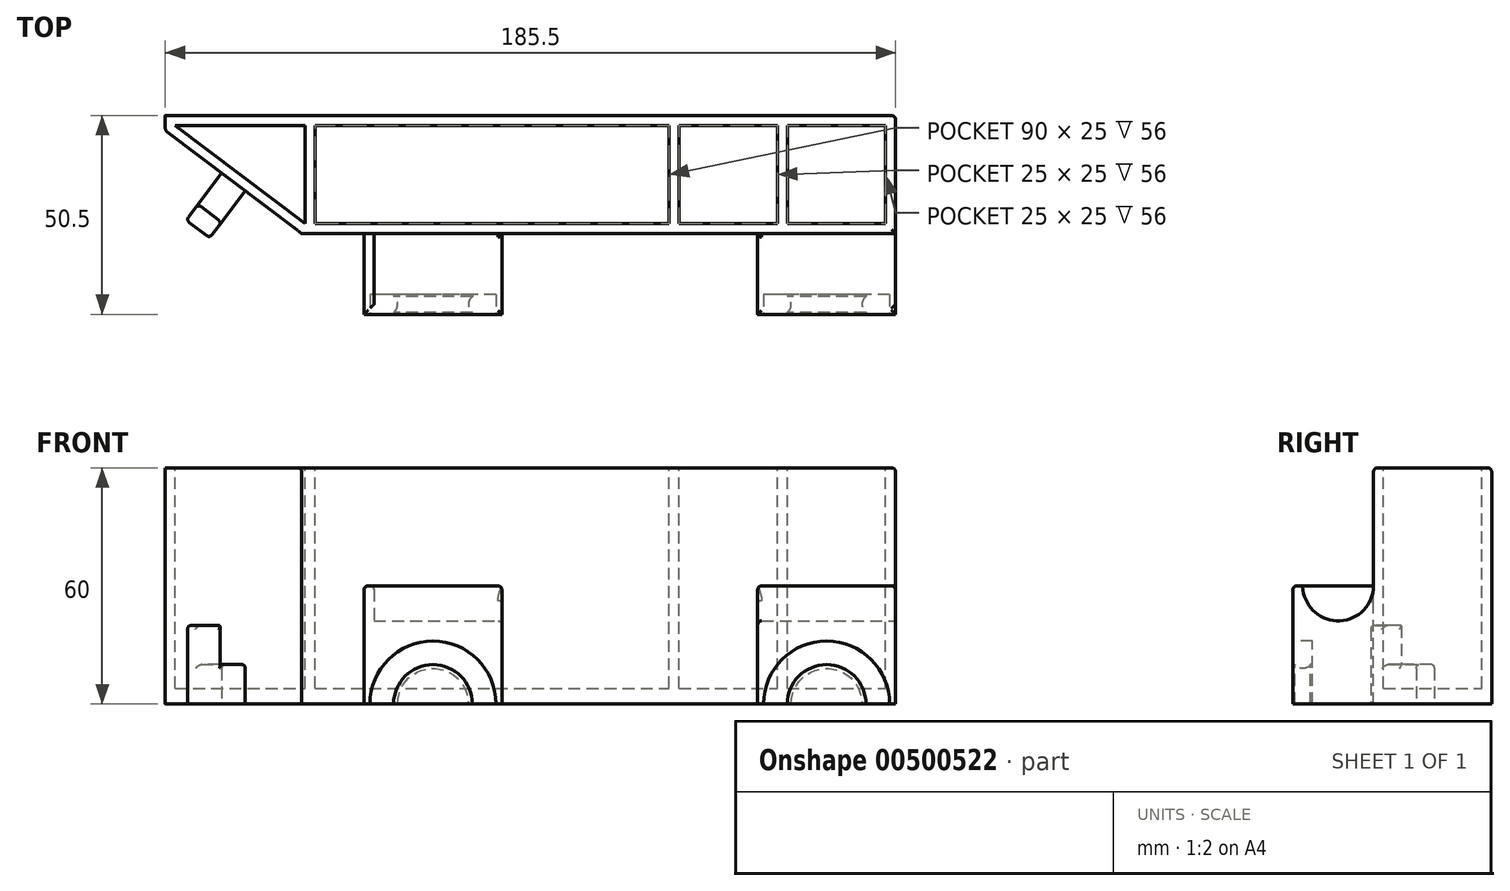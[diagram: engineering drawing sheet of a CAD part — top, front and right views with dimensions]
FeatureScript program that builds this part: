
annotation { "Feature Type Name" : "Feature", "Feature Type Description" : "" }
export const myFeature = defineFeature(function(context is Context, id is Id, definition is map)
    precondition{}
    {
        {
            var Q0;
            Q0=qCreatedBy(makeId("Right.planeOp"),FACE);
            var sketch = newSketch(context, id + "F0", { "sketchPlane" : qUnion([Q0])});
            skLineSegment(sketch, "E0.bottom", {"start": v(0, 0) * mm, "end": v(30, 0) * mm});
            skLineSegment(sketch, "E0.top", {"start": v(0, 60) * mm, "end": v(30, 60) * mm});
            skLineSegment(sketch, "E0.left", {"start": v(0, 0) * mm, "end": v(0, 60) * mm});
            skLineSegment(sketch, "E0.right", {"start": v(30, 0) * mm, "end": v(30, 60) * mm});
            skSolve(sketch);
        }
        {
            var Q0;
            Q0 = qSketchRegion(id + "F0", true);
            extrude(context, id + "F1", {"entities" : qUnion([Q0]), "oppositeDirection" : true, "depth" : 185.5 * mm});
        }
        {
            var Q0;
            Q0=qCreatedBy(makeId("Right.planeOp"),FACE);
            var sketch = newSketch(context, id + "F2", { "sketchPlane" : qUnion([Q0])});
            skLineSegment(sketch, "E1.bottom", {"start": v(0, 0) * mm, "end": v(-20.5, 0) * mm});
            skLineSegment(sketch, "E1.top", {"start": v(0, 30) * mm, "end": v(-20.5, 30) * mm});
            skLineSegment(sketch, "E1.left", {"start": v(0, 0) * mm, "end": v(0, 30) * mm});
            skLineSegment(sketch, "E1.right", {"start": v(-20.5, 0) * mm, "end": v(-20.5, 30) * mm});
            skSolve(sketch);
        }
        {
            var Q0;
            Q0=makeQuery(id+"F2.imprint","IMPRINT",FACE,{"disambiguationData":[TD([[makeQuery(id+"F2.imprint","IMPRINT",EDGE,{"derivedFrom":sQuery(id+"F2.wireOp",EDGE,"E1.bottom")}),-1.0]])]});
            extrude(context, id + "F3", {"entities" : qUnion([Q0]), "operationType" : NewBodyOperationType.ADD, "oppositeDirection" : true, "depth" : 135 * mm});
        }
        {
            var Q0;
            Q0=qCreatedBy(makeId("Top.planeOp"),FACE);
            cPlane(context, id + "F4", {"entities" : qUnion([Q0]), "cplaneType" : CPlaneType.OFFSET, "offset" : 60 * mm, "width" : 150 * mm, "height" : 150 * mm});
        }
        {
            var Q0;
            Q0=qCreatedBy(id+"F4.planeOp",FACE);
            var sketch = newSketch(context, id + "F5", { "sketchPlane" : qUnion([Q0])});
            skLineSegment(sketch, "E2.bottom", {"start": v(-27.5, 27.5) * mm, "end": v(-2.5, 27.5) * mm});
            skLineSegment(sketch, "E2.top", {"start": v(-27.5, 2.5) * mm, "end": v(-2.5, 2.5) * mm});
            skLineSegment(sketch, "E2.left", {"start": v(-27.5, 27.5) * mm, "end": v(-27.5, 2.5) * mm});
            skLineSegment(sketch, "E2.right", {"start": v(-2.5, 27.5) * mm, "end": v(-2.5, 2.5) * mm});
            skLineSegment(sketch, "E3.bottom", {"start": v(-55, 27.5) * mm, "end": v(-30, 27.5) * mm});
            skLineSegment(sketch, "E3.top", {"start": v(-55, 2.5) * mm, "end": v(-30, 2.5) * mm});
            skLineSegment(sketch, "E3.left", {"start": v(-55, 27.5) * mm, "end": v(-55, 2.5) * mm});
            skLineSegment(sketch, "E3.right", {"start": v(-30, 27.5) * mm, "end": v(-30, 2.5) * mm});
            skLineSegment(sketch, "E4.bottom", {"start": v(-147.5, 27.5) * mm, "end": v(-57.5, 27.5) * mm});
            skLineSegment(sketch, "E4.top", {"start": v(-147.5, 2.5) * mm, "end": v(-57.5, 2.5) * mm});
            skLineSegment(sketch, "E4.left", {"start": v(-147.5, 27.5) * mm, "end": v(-147.5, 2.5) * mm});
            skLineSegment(sketch, "E4.right", {"start": v(-57.5, 27.5) * mm, "end": v(-57.5, 2.5) * mm});
            skLineSegment(sketch, "E5", {"start": v(-183, 27.5) * mm, "end": v(-150, 27.5) * mm});
            skLineSegment(sketch, "E6", {"start": v(-150, 27.5) * mm, "end": v(-150, 2.5) * mm});
            skLineSegment(sketch, "E7", {"start": v(-150, 2.5) * mm, "end": v(-183, 27.5) * mm});
            skSolve(sketch);
        }
        {
            var Q0;
            Q0 = qSketchRegion(id + "F5", true);
            extrude(context, id + "F6", {"entities" : qUnion([Q0]), "operationType" : NewBodyOperationType.REMOVE, "oppositeDirection" : true, "depth" : 56 * mm});
        }
        {
            var Q0;
            Q0=qCreatedBy(id+"F4.planeOp",FACE);
            var sketch = newSketch(context, id + "F7", { "sketchPlane" : qUnion([Q0])});
            skLineSegment(sketch, "E8", {"start": v(-187.64, 27.88) * mm, "end": v(-145.34, -4.16) * mm});
            skLineSegment(sketch, "E9", {"start": v(-145.34, -4.16) * mm, "end": v(-187.34, -4.16) * mm});
            skLineSegment(sketch, "E10", {"start": v(-187.34, -4.16) * mm, "end": v(-187.64, 27.88) * mm});
            skSolve(sketch);
        }
        {
            var Q0;
            Q0=makeQuery(id+"F7.imprint","IMPRINT",FACE,{"disambiguationData":[TD([[makeQuery(id+"F7.imprint","IMPRINT",EDGE,{"derivedFrom":sQuery(id+"F7.wireOp",EDGE,"E8")}),-1.0]])]});
            extrude(context, id + "F8", {"entities" : qUnion([Q0]), "operationType" : NewBodyOperationType.REMOVE, "oppositeDirection" : true, "depth" : 93.1 * mm});
        }
        {
            var Q0;
            Q0=qCreatedBy(makeId("Right.planeOp"),FACE);
            var sketch = newSketch(context, id + "F9", { "sketchPlane" : qUnion([Q0])});
            skCircle(sketch, "E11", {"center": v(-9, 30.12) * mm, "radius": 9 * mm});
            skSolve(sketch);
        }
        {
            var Q0;
            Q0 = qSketchRegion(id + "F9", true);
            extrude(context, id + "F10", {"entities" : qUnion([Q0]), "operationType" : NewBodyOperationType.REMOVE, "oppositeDirection" : true, "depth" : 132.5 * mm});
        }
        {
            var Q0;
            Q0=qCreatedBy(id+"F4.planeOp",FACE);
            var sketch = newSketch(context, id + "F11", { "sketchPlane" : qUnion([Q0])});
            skLineSegment(sketch, "E12.bottom", {"start": v(-100, 0) * mm, "end": v(-35, 0) * mm});
            skLineSegment(sketch, "E12.top", {"start": v(-100, -23) * mm, "end": v(-35, -23) * mm});
            skLineSegment(sketch, "E12.left", {"start": v(-100, 0) * mm, "end": v(-100, -23) * mm});
            skLineSegment(sketch, "E12.right", {"start": v(-35, 0) * mm, "end": v(-35, -23) * mm});
            skSolve(sketch);
        }
        {
            var Q0;
            Q0 = qSketchRegion(id + "F11", true);
            extrude(context, id + "F12", {"entities" : qUnion([Q0]), "operationType" : NewBodyOperationType.REMOVE, "oppositeDirection" : true, "depth" : 137 * mm});
        }
        {
            var Q0;
            {var subQ0=sQuery(id+"F2.wireOp",EDGE,"E1.right");Q0=makeQuery(id+"F12.boolean.opBoolean","SPLIT",FACE,{"disambiguationData":[TD([makeQuery(id+"F12.opExtrude","SWEPT_FACE",FACE,{"disambiguationData":[OSD([sQuery(id+"F11.wireOp",EDGE,"E12.right")])]})])],"derivedFrom":makeQuery(id+"F3.opExtrude","SWEPT_FACE",FACE,{"disambiguationData":[OSD([subQ0])]})});}
            cPlane(context, id + "F13", {"entities" : qUnion([Q0]), "cplaneType" : CPlaneType.OFFSET, "offset" : 0 * mm, "width" : 150 * mm, "height" : 150 * mm});
        }
        {
            var Q0;
            Q0=qCreatedBy(id+"F13.planeOp",FACE);
            var sketch = newSketch(context, id + "F14", { "sketchPlane" : qUnion([Q0])});
            skCircle(sketch, "E13", {"center": v(-17.5, 0) * mm, "radius": 16 * mm});
            skCircle(sketch, "E14", {"center": v(-117.5, 0) * mm, "radius": 16 * mm});
            skSolve(sketch);
        }
        {
            var Q0;
            Q0 = qSketchRegion(id + "F14", true);
            extrude(context, id + "F15", {"entities" : qUnion([Q0]), "operationType" : NewBodyOperationType.REMOVE, "oppositeDirection" : true, "depth" : 5 * mm});
        }
        {
            var Q0;
            Q0=qCreatedBy(makeId("Top.planeOp"),FACE);
            var sketch = newSketch(context, id + "F16", { "sketchPlane" : qUnion([Q0])});
            skLineSegment(sketch, "E15.bottom", {"start": v(-17.5, -15.5) * mm, "end": v(-27.5, -15.5) * mm});
            skLineSegment(sketch, "E15.top", {"start": v(-17.5, -20.5) * mm, "end": v(-27.5, -20.5) * mm});
            skLineSegment(sketch, "E15.left", {"start": v(-17.5, -15.5) * mm, "end": v(-17.5, -20.5) * mm});
            skLineSegment(sketch, "E15.right", {"start": v(-27.5, -15.5) * mm, "end": v(-27.5, -16) * mm});
            skArc(sketch, "E16", {"start": v(-27.5, -20) * mm, "mid": v(-26.5, -18) * mm, "end": v(-27.5, -16) * mm});
            skLineSegment(sketch, "E17.trimOffspring", {"start": v(-27.5, -20) * mm, "end": v(-27.5, -20.5) * mm});
            skSolve(sketch);
        }
        {
            var Q0;
            Q0 = qSketchRegion(id + "F16", true);
            var Q1;
            Q1=sQuery(id+"F16.wireOp",EDGE,"E15.left");
            revolve(context, id + "F17", {"operationType" : NewBodyOperationType.ADD, "entities" : qUnion([Q0]), "axis" : qUnion([Q1]), "revolveType" : RevolveType.ONE_DIRECTION, "oppositeDirection" : true, "angle" : 180 * degree});
        }
        {
            var Q0;
            Q0=qCreatedBy(makeId("Top.planeOp"),FACE);
            var sketch = newSketch(context, id + "F18", { "sketchPlane" : qUnion([Q0])});
            skLineSegment(sketch, "E18.bottom", {"start": v(-117.5, -15.5) * mm, "end": v(-127.5, -15.5) * mm});
            skLineSegment(sketch, "E18.top", {"start": v(-117.5, -20.5) * mm, "end": v(-127.5, -20.5) * mm});
            skLineSegment(sketch, "E18.left", {"start": v(-117.5, -15.5) * mm, "end": v(-117.5, -20.5) * mm});
            skLineSegment(sketch, "E18.right", {"start": v(-127.5, -15.5) * mm, "end": v(-127.5, -16) * mm});
            skArc(sketch, "E19", {"start": v(-127.5, -20) * mm, "mid": v(-126.5, -18) * mm, "end": v(-127.5, -16) * mm});
            skLineSegment(sketch, "E20.trimOffspring", {"start": v(-127.5, -20) * mm, "end": v(-127.5, -20.5) * mm});
            skSolve(sketch);
        }
        {
            var Q0;
            Q0 = qSketchRegion(id + "F18", true);
            var Q1;
            Q1=sQuery(id+"F18.wireOp",EDGE,"E18.left");
            revolve(context, id + "F19", {"operationType" : NewBodyOperationType.ADD, "entities" : qUnion([Q0]), "axis" : qUnion([Q1]), "revolveType" : RevolveType.ONE_DIRECTION, "oppositeDirection" : true, "angle" : 180 * degree});
        }
        {
            var Q0;
            Q0=qCreatedBy(makeId("Top.planeOp"),FACE);
            var sketch = newSketch(context, id + "F20", { "sketchPlane" : qUnion([Q0])});
            skLineSegment(sketch, "E21", {"start": v(-171.16, 15.4) * mm, "end": v(-180.22, 3.44) * mm});
            skLineSegment(sketch, "E22", {"start": v(-180.22, 3.44) * mm, "end": v(-174.24, -1.1) * mm});
            skLineSegment(sketch, "E23", {"start": v(-174.24, -1.1) * mm, "end": v(-165.18, 10.86) * mm});
            skLineSegment(sketch, "E24", {"start": v(-165.18, 10.86) * mm, "end": v(-171.16, 15.4) * mm});
            skSolve(sketch);
        }
        {
            var Q0;
            Q0=makeQuery(id+"F20.imprint","IMPRINT",FACE,{"disambiguationData":[TD([[makeQuery(id+"F20.imprint","IMPRINT",EDGE,{"derivedFrom":sQuery(id+"F20.wireOp",EDGE,"E21")}),1.0]])]});
            extrude(context, id + "F21", {"entities" : qUnion([Q0]), "operationType" : NewBodyOperationType.ADD, "depth" : 20 * mm});
        }
        {
            var Q0;
            Q0=makeQuery(id+"F1.opExtrude","SWEPT_EDGE",EDGE,{"disambiguationData":[OSD([sQuery(id+"F0.wireOp",EDGE,"E0.top"),sQuery(id+"F0.wireOp",EDGE,"E0.right")])]});
            var Q1;
            Q1=makeQuery(id+"F6.boolean.opBoolean","COPY",EDGE,{"derivedFrom":makeQuery(id+"F6.opExtrude","CAP_EDGE",EDGE,{"disambiguationData":[OSD([sQuery(id+"F5.wireOp",EDGE,"E4.left")])],"isStart":true})});
            var Q2;
            Q2=makeQuery(id+"F6.boolean.opBoolean","COPY",EDGE,{"derivedFrom":makeQuery(id+"F6.opExtrude","CAP_EDGE",EDGE,{"disambiguationData":[OSD([sQuery(id+"F5.wireOp",EDGE,"E4.bottom")])],"isStart":true})});
            var Q3;
            Q3=makeQuery(id+"F6.boolean.opBoolean","COPY",EDGE,{"derivedFrom":makeQuery(id+"F6.opExtrude","CAP_EDGE",EDGE,{"disambiguationData":[OSD([sQuery(id+"F5.wireOp",EDGE,"E4.top")])],"isStart":true})});
            var Q4;
            Q4=makeQuery(id+"F6.boolean.opBoolean","COPY",EDGE,{"derivedFrom":makeQuery(id+"F6.opExtrude","CAP_EDGE",EDGE,{"disambiguationData":[OSD([sQuery(id+"F5.wireOp",EDGE,"E4.right")])],"isStart":true})});
            var Q5;
            Q5=makeQuery(id+"F6.boolean.opBoolean","COPY",EDGE,{"derivedFrom":makeQuery(id+"F6.opExtrude","CAP_EDGE",EDGE,{"disambiguationData":[OSD([sQuery(id+"F5.wireOp",EDGE,"E3.top")])],"isStart":true})});
            var Q6;
            Q6=makeQuery(id+"F6.boolean.opBoolean","COPY",EDGE,{"derivedFrom":makeQuery(id+"F6.opExtrude","CAP_EDGE",EDGE,{"disambiguationData":[OSD([sQuery(id+"F5.wireOp",EDGE,"E3.right")])],"isStart":true})});
            var Q7;
            Q7=makeQuery(id+"F6.boolean.opBoolean","COPY",EDGE,{"derivedFrom":makeQuery(id+"F6.opExtrude","CAP_EDGE",EDGE,{"disambiguationData":[OSD([sQuery(id+"F5.wireOp",EDGE,"E3.bottom")])],"isStart":true})});
            var Q8;
            Q8=makeQuery(id+"F6.boolean.opBoolean","COPY",EDGE,{"derivedFrom":makeQuery(id+"F6.opExtrude","CAP_EDGE",EDGE,{"disambiguationData":[OSD([sQuery(id+"F5.wireOp",EDGE,"E3.left")])],"isStart":true})});
            var Q9;
            Q9=makeQuery(id+"F6.boolean.opBoolean","COPY",EDGE,{"derivedFrom":makeQuery(id+"F6.opExtrude","CAP_EDGE",EDGE,{"disambiguationData":[OSD([sQuery(id+"F5.wireOp",EDGE,"E2.left")])],"isStart":true})});
            var Q10;
            Q10=makeQuery(id+"F6.boolean.opBoolean","COPY",EDGE,{"derivedFrom":makeQuery(id+"F6.opExtrude","CAP_EDGE",EDGE,{"disambiguationData":[OSD([sQuery(id+"F5.wireOp",EDGE,"E2.bottom")])],"isStart":true})});
            var Q11;
            Q11=makeQuery(id+"F6.boolean.opBoolean","COPY",EDGE,{"derivedFrom":makeQuery(id+"F6.opExtrude","CAP_EDGE",EDGE,{"disambiguationData":[OSD([sQuery(id+"F5.wireOp",EDGE,"E2.right")])],"isStart":true})});
            var Q12;
            Q12=makeQuery(id+"F6.boolean.opBoolean","COPY",EDGE,{"derivedFrom":makeQuery(id+"F6.opExtrude","CAP_EDGE",EDGE,{"disambiguationData":[OSD([sQuery(id+"F5.wireOp",EDGE,"E2.top")])],"isStart":true})});
            var Q13;
            Q13=makeQuery(id+"F6.boolean.opBoolean","COPY",EDGE,{"derivedFrom":makeQuery(id+"F6.opExtrude","CAP_EDGE",EDGE,{"disambiguationData":[OSD([sQuery(id+"F5.wireOp",EDGE,"E7")])],"isStart":true})});
            var Q14;
            Q14=makeQuery(id+"F6.boolean.opBoolean","COPY",EDGE,{"derivedFrom":makeQuery(id+"F6.opExtrude","CAP_EDGE",EDGE,{"disambiguationData":[OSD([sQuery(id+"F5.wireOp",EDGE,"E6")])],"isStart":true})});
            var Q15;
            Q15=makeQuery(id+"F6.boolean.opBoolean","COPY",EDGE,{"derivedFrom":makeQuery(id+"F6.opExtrude","CAP_EDGE",EDGE,{"disambiguationData":[OSD([sQuery(id+"F5.wireOp",EDGE,"E5")])],"isStart":true})});
            var Q16;
            Q16=makeQuery(id+"F10.boolean.opBoolean","INTERSECT",EDGE,{"derivedFrom":[makeQuery(id+"F3.opExtrude","SWEPT_FACE",FACE,{"disambiguationData":[OSD([sQuery(id+"F2.wireOp",EDGE,"E1.top")])]}),makeQuery(id+"F10.opExtrude","CAP_FACE",FACE,{"disambiguationData":[OSD([sQuery(id+"F9.wireOp",EDGE,"E11")])],"isStart":false})]});
            var Q17;
            Q17=makeQuery(id+"F3.opExtrude","CAP_EDGE",EDGE,{"disambiguationData":[OSD([sQuery(id+"F2.wireOp",EDGE,"E1.top")])],"isStart":false});
            var Q18;
            {var subQ0=sQuery(id+"F2.wireOp",EDGE,"E1.right");var subQ1=sQuery(id+"F2.wireOp",EDGE,"E1.top");Q18=makeQuery(id+"F12.boolean.opBoolean","SPLIT",EDGE,{"disambiguationData":[TD([makeQuery(id+"F12.opExtrude","SWEPT_FACE",FACE,{"disambiguationData":[OSD([sQuery(id+"F11.wireOp",EDGE,"E12.left")])]})])],"derivedFrom":makeQuery(id+"F3.opExtrude","SWEPT_EDGE",EDGE,{"disambiguationData":[OSD([subQ1,subQ0])]})});}
            var Q19;
            {var subQ0=makeQuery(id+"F3.opExtrude","SWEPT_FACE",FACE,{"disambiguationData":[OSD([sQuery(id+"F2.wireOp",EDGE,"E1.top")])]});var subQ1=sQuery(id+"F9.wireOp",EDGE,"E11");var subQ2=makeQuery(id+"F10.opExtrude","SWEPT_FACE",FACE,{"disambiguationData":[OSD([subQ1])]});Q19=makeQuery(id+"F12.boolean.opBoolean","SPLIT",EDGE,{"disambiguationData":[TD([makeQuery(id+"F10.boolean.opBoolean","COPY",FACE,{"derivedFrom":makeQuery(id+"F10.opExtrude","CAP_FACE",FACE,{"disambiguationData":[OSD([subQ1])],"isStart":false})})])],"derivedFrom":makeQuery(id+"F10.boolean.opBoolean","INTERSECT",EDGE,{"disambiguationData":[OD(0.0)],"derivedFrom":[subQ0,subQ2]})});}
            var Q20;
            {var subQ0=makeQuery(id+"F10.opExtrude","SWEPT_FACE",FACE,{"disambiguationData":[OSD([sQuery(id+"F9.wireOp",EDGE,"E11")])]});var subQ1=sQuery(id+"F2.wireOp",EDGE,"E1.top");var subQ2=makeQuery(id+"F3.opExtrude","SWEPT_FACE",FACE,{"disambiguationData":[OSD([subQ1])]});Q20=makeQuery(id+"F12.boolean.opBoolean","SPLIT",EDGE,{"disambiguationData":[TD([makeQuery(id+"F12.opExtrude","SWEPT_FACE",FACE,{"disambiguationData":[OSD([sQuery(id+"F11.wireOp",EDGE,"E12.right")])]})])],"derivedFrom":makeQuery(id+"F10.boolean.opBoolean","INTERSECT",EDGE,{"disambiguationData":[OD(0.0)],"derivedFrom":[subQ2,subQ0]})});}
            var Q21;
            {var subQ0=sQuery(id+"F2.wireOp",EDGE,"E1.right");var subQ1=sQuery(id+"F2.wireOp",EDGE,"E1.top");Q21=makeQuery(id+"F12.boolean.opBoolean","SPLIT",FACE,{"disambiguationData":[TD([makeQuery(id+"F1.opExtrude","CAP_FACE",FACE,{"disambiguationData":[OSD([sQuery(id+"F0.wireOp",EDGE,"E0.bottom"),sQuery(id+"F0.wireOp",EDGE,"E0.top"),sQuery(id+"F0.wireOp",EDGE,"E0.left"),sQuery(id+"F0.wireOp",EDGE,"E0.right")])],"isStart":true}),makeQuery(id+"F3.opExtrude","CAP_FACE",FACE,{"disambiguationData":[OSD([sQuery(id+"F2.wireOp",EDGE,"E1.bottom"),subQ1,sQuery(id+"F2.wireOp",EDGE,"E1.left"),subQ0])],"isStart":true}),makeQuery(id+"F3.opExtrude","SWEPT_FACE",FACE,{"disambiguationData":[OSD([subQ0])]}),makeQuery(id+"F10.boolean.opBoolean","COPY",FACE,{"derivedFrom":makeQuery(id+"F10.opExtrude","SWEPT_FACE",FACE,{"disambiguationData":[OSD([sQuery(id+"F9.wireOp",EDGE,"E11")])]})}),makeQuery(id+"F12.opExtrude","SWEPT_FACE",FACE,{"disambiguationData":[OSD([sQuery(id+"F11.wireOp",EDGE,"E12.right")])]})])],"derivedFrom":makeQuery(id+"F3.opExtrude","SWEPT_FACE",FACE,{"disambiguationData":[OSD([subQ1])]})});}
            var Q22;
            Q22=makeQuery(id+"F12.boolean.opBoolean","INTERSECT",EDGE,{"disambiguationData":[OD(1.0)],"derivedFrom":[makeQuery(id+"F3.opExtrude","SWEPT_FACE",FACE,{"disambiguationData":[OSD([sQuery(id+"F2.wireOp",EDGE,"E1.top")])]}),makeQuery(id+"F12.opExtrude","SWEPT_FACE",FACE,{"disambiguationData":[OSD([sQuery(id+"F11.wireOp",EDGE,"E12.right")])]})]});
            var Q23;
            Q23=makeQuery(id+"F12.boolean.opBoolean","INTERSECT",EDGE,{"disambiguationData":[OD(1.0)],"derivedFrom":[makeQuery(id+"F3.opExtrude","SWEPT_FACE",FACE,{"disambiguationData":[OSD([sQuery(id+"F2.wireOp",EDGE,"E1.top")])]}),makeQuery(id+"F12.opExtrude","SWEPT_FACE",FACE,{"disambiguationData":[OSD([sQuery(id+"F11.wireOp",EDGE,"E12.left")])]})]});
            fillet(context, id + "F22", {"entities" : qUnion([Q0, Q1, Q2, Q3, Q4, Q5, Q6, Q7, Q8, Q9, Q10, Q11, Q12, Q13, Q14, Q15, Q16, Q17, Q18, Q19, Q20, Q21, Q22, Q23]), "radius" : 1 * mm, "tangentPropagation" : true, "allowEdgeOverflow" : false});
        }
        {
            var Q0;
            Q0=makeQuery(id+"F8.boolean.opBoolean","COPY",EDGE,{"derivedFrom":makeQuery(id+"F8.opExtrude","CAP_EDGE",EDGE,{"disambiguationData":[OSD([sQuery(id+"F7.wireOp",EDGE,"E8")])],"isStart":true})});
            var Q1;
            Q1=makeQuery(id+"F1.opExtrude","SWEPT_EDGE",EDGE,{"disambiguationData":[OSD([sQuery(id+"F0.wireOp",EDGE,"E0.top"),sQuery(id+"F0.wireOp",EDGE,"E0.left")])]});
            var Q2;
            Q2=makeQuery(id+"F1.opExtrude","CAP_EDGE",EDGE,{"disambiguationData":[OSD([sQuery(id+"F0.wireOp",EDGE,"E0.top")])],"isStart":true});
            fillet(context, id + "F23", {"entities" : qUnion([Q0, Q1, Q2]), "radius" : 1 * mm, "tangentPropagation" : true, "allowEdgeOverflow" : false});
        }
        {
            var Q0;
            Q0=makeQuery(id+"F8.boolean.opBoolean","INTERSECT",EDGE,{"derivedFrom":[makeQuery(id+"F1.opExtrude","CAP_FACE",FACE,{"disambiguationData":[OSD([sQuery(id+"F0.wireOp",EDGE,"E0.bottom"),sQuery(id+"F0.wireOp",EDGE,"E0.top"),sQuery(id+"F0.wireOp",EDGE,"E0.left"),sQuery(id+"F0.wireOp",EDGE,"E0.right")])],"isStart":false}),makeQuery(id+"F8.opExtrude","SWEPT_FACE",FACE,{"disambiguationData":[OSD([sQuery(id+"F7.wireOp",EDGE,"E8")])]})]});
            var Q1;
            Q1=makeQuery(id+"F12.boolean.opBoolean","INTERSECT",EDGE,{"derivedFrom":[makeQuery(id+"F10.boolean.opBoolean","COPY",FACE,{"derivedFrom":makeQuery(id+"F10.opExtrude","SWEPT_FACE",FACE,{"disambiguationData":[OSD([sQuery(id+"F9.wireOp",EDGE,"E11")])]})}),makeQuery(id+"F12.opExtrude","SWEPT_FACE",FACE,{"disambiguationData":[OSD([sQuery(id+"F11.wireOp",EDGE,"E12.left")])]})]});
            var Q2;
            Q2=makeQuery(id+"F12.boolean.opBoolean","INTERSECT",EDGE,{"derivedFrom":[makeQuery(id+"F10.boolean.opBoolean","COPY",FACE,{"derivedFrom":makeQuery(id+"F10.opExtrude","SWEPT_FACE",FACE,{"disambiguationData":[OSD([sQuery(id+"F9.wireOp",EDGE,"E11")])]})}),makeQuery(id+"F12.opExtrude","SWEPT_FACE",FACE,{"disambiguationData":[OSD([sQuery(id+"F11.wireOp",EDGE,"E12.right")])]})]});
            fillet(context, id + "F24", {"entities" : qUnion([Q0, Q1, Q2]), "radius" : 1 * mm, "tangentPropagation" : true, "allowEdgeOverflow" : false});
        }
        {
            var Q0;
            Q0=makeQuery(id+"F19.opRevolve","SWEPT_EDGE",EDGE,{"disambiguationData":[OSD([sQuery(id+"F18.wireOp",EDGE,"E18.top"),sQuery(id+"F18.wireOp",EDGE,"E20.trimOffspring")])]});
            var Q1;
            Q1=makeQuery(id+"F17.opRevolve","SWEPT_EDGE",EDGE,{"disambiguationData":[OSD([sQuery(id+"F16.wireOp",EDGE,"E15.top"),sQuery(id+"F16.wireOp",EDGE,"E17.trimOffspring")])]});
            fillet(context, id + "F25", {"entities" : qUnion([Q0, Q1]), "radius" : 5 * mm, "tangentPropagation" : true, "allowEdgeOverflow" : false});
        }
        {
            var Q0;
            Q0=makeQuery(id+"F21.opExtrude","CAP_FACE",FACE,{"disambiguationData":[OSD([sQuery(id+"F20.wireOp",EDGE,"E21"),sQuery(id+"F20.wireOp",EDGE,"E22"),sQuery(id+"F20.wireOp",EDGE,"E23"),sQuery(id+"F20.wireOp",EDGE,"E24")])],"isStart":false});
            cPlane(context, id + "F26", {"entities" : qUnion([Q0]), "cplaneType" : CPlaneType.OFFSET, "offset" : 0 * mm, "width" : 150 * mm, "height" : 150 * mm});
        }
        {
            var Q0;
            Q0=qCreatedBy(id+"F26.planeOp",FACE);
            var sketch = newSketch(context, id + "F27", { "sketchPlane" : qUnion([Q0])});
            skLineSegment(sketch, "E25", {"start": v(-175.65, 18.8) * mm, "end": v(-161.36, 7.97) * mm});
            skLineSegment(sketch, "E26", {"start": v(-175.65, 18.8) * mm, "end": v(-181.69, 10.82) * mm});
            skLineSegment(sketch, "E27", {"start": v(-181.69, 10.82) * mm, "end": v(-167.4, 0) * mm});
            skLineSegment(sketch, "E28", {"start": v(-167.4, 0) * mm, "end": v(-161.36, 7.97) * mm});
            skSolve(sketch);
        }
        {
            var Q0;
            Q0 = qSketchRegion(id + "F27", true);
            extrude(context, id + "F28", {"entities" : qUnion([Q0]), "operationType" : NewBodyOperationType.REMOVE, "oppositeDirection" : true, "depth" : 10 * mm});
        }
        {
            var Q0;
            Q0=makeQuery(id+"F21.opExtrude","SWEPT_EDGE",EDGE,{"disambiguationData":[OSD([sQuery(id+"F20.wireOp",EDGE,"E21"),sQuery(id+"F20.wireOp",EDGE,"E22")])]});
            var Q1;
            Q1=makeQuery(id+"F28.boolean.opBoolean","COPY",EDGE,{"derivedFrom":makeQuery(id+"F28.opExtrude","CAP_EDGE",EDGE,{"disambiguationData":[OSD([sQuery(id+"F27.wireOp",EDGE,"E27")])],"isStart":true})});
            var Q2;
            Q2=makeQuery(id+"F21.opExtrude","CAP_EDGE",EDGE,{"disambiguationData":[OSD([sQuery(id+"F20.wireOp",EDGE,"E21")])],"isStart":false});
            var Q3;
            Q3=makeQuery(id+"F28.boolean.opBoolean","INTERSECT",EDGE,{"derivedFrom":[makeQuery(id+"F21.opExtrude","SWEPT_FACE",FACE,{"disambiguationData":[OSD([sQuery(id+"F20.wireOp",EDGE,"E21")])]}),makeQuery(id+"F28.opExtrude","SWEPT_FACE",FACE,{"disambiguationData":[OSD([sQuery(id+"F27.wireOp",EDGE,"E27")])]})]});
            var Q4;
            Q4=makeQuery(id+"F21.opExtrude","CAP_EDGE",EDGE,{"disambiguationData":[OSD([sQuery(id+"F20.wireOp",EDGE,"E23")])],"isStart":false});
            var Q5;
            Q5=makeQuery(id+"F21.opExtrude","CAP_EDGE",EDGE,{"disambiguationData":[OSD([sQuery(id+"F20.wireOp",EDGE,"E22")])],"isStart":false});
            var Q6;
            Q6=makeQuery(id+"F28.boolean.opBoolean","INTERSECT",EDGE,{"derivedFrom":[makeQuery(id+"F21.opExtrude","SWEPT_FACE",FACE,{"disambiguationData":[OSD([sQuery(id+"F20.wireOp",EDGE,"E23")])]}),makeQuery(id+"F28.opExtrude","CAP_FACE",FACE,{"disambiguationData":[OSD([sQuery(id+"F27.wireOp",EDGE,"E25"),sQuery(id+"F27.wireOp",EDGE,"E26"),sQuery(id+"F27.wireOp",EDGE,"E27"),sQuery(id+"F27.wireOp",EDGE,"E28")])],"isStart":false})]});
            var Q7;
            Q7=makeQuery(id+"F28.boolean.opBoolean","INTERSECT",EDGE,{"derivedFrom":[makeQuery(id+"F21.opExtrude","SWEPT_FACE",FACE,{"disambiguationData":[OSD([sQuery(id+"F20.wireOp",EDGE,"E23")])]}),makeQuery(id+"F28.opExtrude","SWEPT_FACE",FACE,{"disambiguationData":[OSD([sQuery(id+"F27.wireOp",EDGE,"E27")])]})]});
            var Q8;
            Q8=makeQuery(id+"F21.opExtrude","SWEPT_EDGE",EDGE,{"disambiguationData":[OSD([sQuery(id+"F20.wireOp",EDGE,"E22"),sQuery(id+"F20.wireOp",EDGE,"E23")])]});
            var Q9;
            Q9=makeQuery(id+"F28.boolean.opBoolean","INTERSECT",EDGE,{"derivedFrom":[makeQuery(id+"F21.opExtrude","SWEPT_FACE",FACE,{"disambiguationData":[OSD([sQuery(id+"F20.wireOp",EDGE,"E21")])]}),makeQuery(id+"F28.opExtrude","CAP_FACE",FACE,{"disambiguationData":[OSD([sQuery(id+"F27.wireOp",EDGE,"E25"),sQuery(id+"F27.wireOp",EDGE,"E26"),sQuery(id+"F27.wireOp",EDGE,"E27"),sQuery(id+"F27.wireOp",EDGE,"E28")])],"isStart":false})]});
            fillet(context, id + "F29", {"entities" : qUnion([Q0, Q1, Q2, Q3, Q4, Q5, Q6, Q7, Q8, Q9]), "radius" : 1 * mm, "tangentPropagation" : true, "allowEdgeOverflow" : false});
        }
    });
